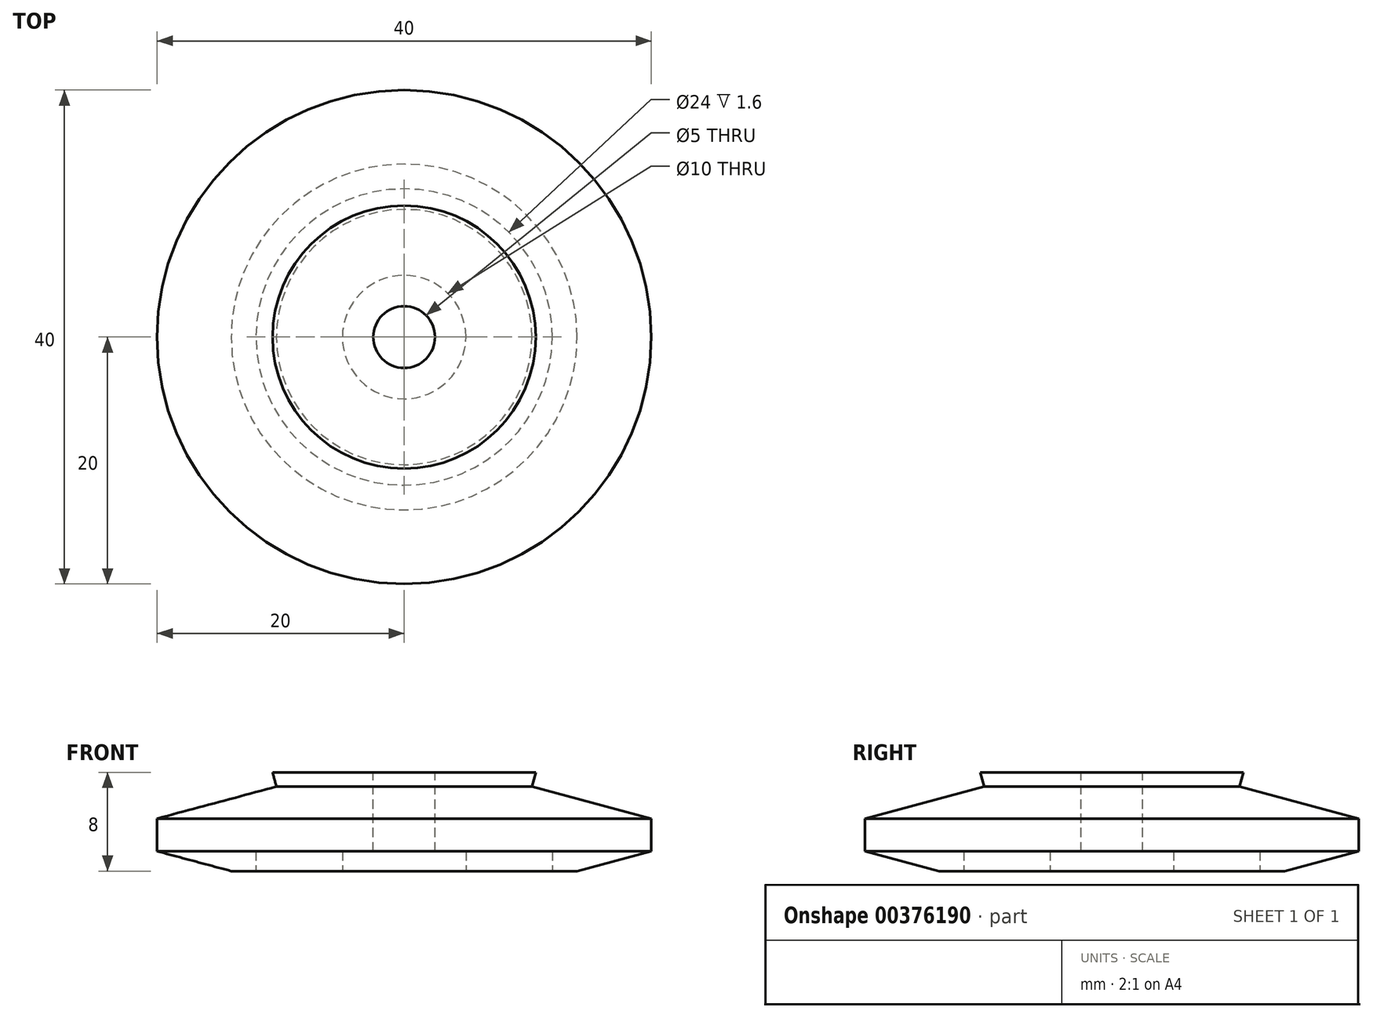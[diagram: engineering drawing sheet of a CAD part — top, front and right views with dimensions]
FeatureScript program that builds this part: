
annotation { "Feature Type Name" : "Feature", "Feature Type Description" : "" }
export const myFeature = defineFeature(function(context is Context, id is Id, definition is map)
    precondition{}
    {
        {
            var Q0;
            Q0=qCreatedBy(makeId("Front.planeOp"),FACE);
            var sketch = newSketch(context, id + "F0", { "sketchPlane" : qUnion([Q0])});
            skLineSegment(sketch, "E0", {"start": v(0, 0) * mm, "end": v(20, 0) * mm});
            skLineSegment(sketch, "E1", {"start": v(20, 0) * mm, "end": v(20, 4.25) * mm});
            skLineSegment(sketch, "E2", {"start": v(0, 0) * mm, "end": v(0, 8) * mm});
            skLineSegment(sketch, "E3", {"start": v(0, 8) * mm, "end": v(6.01, 8) * mm});
            skLineSegment(sketch, "E4", {"start": v(20, 4.25) * mm, "end": v(6.01, 8) * mm});
            skLineSegment(sketch, "E5", {"start": v(6.01, 8) * mm, "end": v(10.65, 8) * mm});
            skLineSegment(sketch, "E6", {"start": v(10.34, 6.84) * mm, "end": v(10.65, 8) * mm});
            skLineSegment(sketch, "E7", {"start": v(0, 0) * mm, "end": v(0, 1.6) * mm});
            skLineSegment(sketch, "E8", {"start": v(12, 1.6) * mm, "end": v(0, 1.6) * mm});
            skLineSegment(sketch, "E9", {"start": v(12, 1.6) * mm, "end": v(12, 0) * mm});
            skLineSegment(sketch, "E10", {"start": v(3, 8) * mm, "end": v(3, 0) * mm, "construction": true});
            skLineSegment(sketch, "E11", {"start": v(14, 0) * mm, "end": v(20, 1.6) * mm});
            skLineSegment(sketch, "E12", {"start": v(5, 1.6) * mm, "end": v(5, 0) * mm});
            skSolve(sketch);
        }
        {
            var Q0;
            {var subQ0=sQuery(id+"F0.wireOp",EDGE,"E9");Q0=makeQuery(id+"F0.imprint","IMPRINT",FACE,{"disambiguationData":[TD([[makeQuery(id+"F0.imprint","IMPRINT",EDGE,{"derivedFrom":subQ0}),-1.0]])]});}
            var Q1;
            Q1=sQuery(id+"F0.wireOp",EDGE,"E7");
            revolve(context, id + "F1", {"entities" : qUnion([Q0]), "axis" : qUnion([Q1]), "revolveType" : RevolveType.FULL});
        }
        {
            var Q0;
            {var subQ9=sQuery(id+"F0.wireOp",EDGE,"E9");Q0=makeQuery(id+"F0.imprint","IMPRINT",FACE,{"disambiguationData":[TD([[makeQuery(id+"F0.imprint","IMPRINT",EDGE,{"derivedFrom":subQ9}),1.0]])]});}
            var Q1;
            {var subQ0=sQuery(id+"F0.wireOp",EDGE,"E7");Q1=makeQuery(id+"F0.imprint","IMPRINT",FACE,{"disambiguationData":[TD([[makeQuery(id+"F0.imprint","IMPRINT",EDGE,{"derivedFrom":subQ0}),-1.0]])]});}
            var Q2;
            {var subQ0=sQuery(id+"F0.wireOp",EDGE,"E5");Q2=makeQuery(id+"F0.imprint","IMPRINT",FACE,{"disambiguationData":[TD([[makeQuery(id+"F0.imprint","IMPRINT",EDGE,{"derivedFrom":subQ0}),-1.0]])]});}
            var Q3;
            Q3=sQuery(id+"F0.wireOp",EDGE,"E2");
            revolve(context, id + "F2", {"entities" : qUnion([Q0, Q1, Q2]), "axis" : qUnion([Q3]), "revolveType" : RevolveType.FULL});
        }
        {
            var Q0;
            Q0=makeQuery(id+"F2.opRevolve","SWEPT_FACE",FACE,{"disambiguationData":[OSD([sQuery(id+"F0.wireOp",EDGE,"E3"),sQuery(id+"F0.wireOp",EDGE,"E5")])]});
            var sketch = newSketch(context, id + "F3", { "sketchPlane" : qUnion([Q0])});
            skPoint(sketch, "E13", {"position": v(0, 7) * mm});
            skPoint(sketch, "E14.MirrorP", {"position": v(0, -7) * mm});
            skPoint(sketch, "E15", {"position": v(-9, 0) * mm});
            skPoint(sketch, "E16.MirrorP", {"position": v(9, 0) * mm});
            skPoint(sketch, "E17", {"position": v(0, 0) * mm});
            skSolve(sketch);
        }
        {
            var Q0;
            Q0=sQuery(id+"F3.wireOp",VERTEX,"E17");
            var Q1;
            Q1=makeQuery(id+"F2.opRevolve","SWEPT_BODY",BODY,{"disambiguationData":[OSD([sQuery(id+"F0.wireOp",EDGE,"E0"),sQuery(id+"F0.wireOp",EDGE,"E1"),sQuery(id+"F0.wireOp",EDGE,"E2"),sQuery(id+"F0.wireOp",EDGE,"E3"),sQuery(id+"F0.wireOp",EDGE,"E4"),sQuery(id+"F0.wireOp",EDGE,"E5"),sQuery(id+"F0.wireOp",EDGE,"E6"),sQuery(id+"F0.wireOp",EDGE,"E8"),sQuery(id+"F0.wireOp",EDGE,"E9"),sQuery(id+"F0.wireOp",EDGE,"E11")])]});
            hole(context, id + "F4", {"style" : HoleStyle.SIMPLE, "endStyle" : HoleEndStyle.THROUGH, "standardTappedOrClearance" : lookupTablePath({ "standard" : "ISO", "engagement" : "75%", "pitch" : "1 mm", "size" : "M6", "type" : "Tapped" }), "standardBlindInLast" : lookupTablePath({ "standard" : "ISO", "engagement" : "75%", "pitch" : "1 mm", "size" : "M6", "type" : "Tapped" }), "holeDiameter" : 5 * mm, "showTappedDepth" : true, "isTappedThrough" : true, "tappedDepth" : 35 * mm, "tapClearance" : 3, "startFromSketch" : true, "locations" : qUnion([Q0]), "scope" : qUnion([Q1]), "majorDiameter" : 6 * mm});
        }
    });
